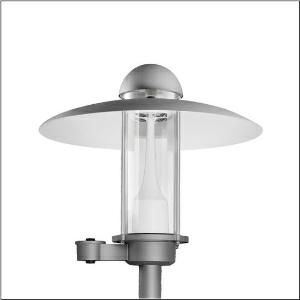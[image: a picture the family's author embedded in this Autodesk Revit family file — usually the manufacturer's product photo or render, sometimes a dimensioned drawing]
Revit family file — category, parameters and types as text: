
# Revit family: city-light_elegance___st1_2a_5xa5263er14h000032_c7d7
name_source: partatom
category: Lighting Fixtures
units: mm (PartAtom-declared; Revit-internal decimal feet)

## family parameters
Cut with Voids When Loaded = No
Host = Face
Light Source = No
Part Type = Normal
Room Calculation Point = No
Round Connector Dimension = Use Diameter
Shared = No

## types (1)
- --- (1 x LED, 1470 lm, 14.2 W, 3000K)
    Apparent Load = 14 VA
    CIE Flux Codes = 22 62 94 98 100
    Color Rendering = 80
    Color Temperature = 3000K
    Default Elevation = 1800 mm
    Description = City-Light Elegance, mast luminaire, Module 540 Plus, primary light control with 3 zone facetted reflector, of plastic, silver coated, highly specular, structured, primary optical cover: cover, of PMMA, transparent, light distribution: ST1.2a, light emission: direct distribution, primary light characteristic: asymmetric, installation type: post-top, LED, High Power LED, rated luminous flux: 1.470lm, luminous efficacy: 104lm/W, light colour: 830, colour temperature: 3000K, control gear: ECG Smart Interface, control: overheat protection, digital communication interface, time-dependent luminous flux control, flexible luminous flux parameterisation, presetting dimming logarithmic, with terminal, 6-pole, max. 2.5mm², mains connection: 230..240V, AC, 50/60Hz, start of lifetime: 14W, end of service life: 15W, reduction: 8W, luminaire housing, upper part, of aluminium, coated, Siteco® metallic grey (DB 702S), diameter: 750mm, height: 675mm, spigot size: d x l = 76 x 70mm (post-top) | with reducer (optional accessory) 60 x 70mm, post-top mast mounting element, of diecast aluminium, coated, Siteco® metallic grey (DB 702S), Module 540 Plus, traffic white (RAL 9016), Smart Interface below, protection rating (complete): IP65, insulation class (complete): insulation class II (safety insulation), certification: CE, ENEC, VDE, packaging unit: 1 piece

Light Distribution: ST1.2a
    Height = 675 mm
    Lamp = 1 x LED
    Lamp Light Flux = 1470 lm
    Lamp Power = 14.2 W
    Lamp count = 1
    Length = 750 mm
    Luminous efficacy = 104 lm/W
    Manufacturer = Siteco
    ModVariant = No
    Model = 5XA5263ER14H000032
    Number of Poles = 1
    OnlyDefault = Yes
    Power Factor = 1
    Product Name = City-Light Elegance | ST1.2a
    Product group = mast luminaire | pylon top
    ProductGroupID = 6100
    Protection Class = Protection class II
    Protection Degree = IP 65
    RLX_Detail_Level = 1
    RLX_Emergency_Light_Flux = 0 lm
    RLX_Emergency_Type = 0
    RLX_Emergency_Type_DB = No
    RlxData = <blob elided: 72729 chars, md5=fc4e0b91>
    Socket = socket
    Standby Power = 0 W
    System Light Flux = 1470 lm
    System Power = 14 W
    Type Comments = factory setting: luminous flux: 100 % | dim-lin: 254 | 516 mA
    Type Image = l_1005991.jpg
    URL = http://relux.com
    VarID = @adj_151447
    Voltage = 0 V
    Weight = 0.00 kg
    Width = 0 mm  [stored 0 ft]

note: [stored X ft] marks values corroborated as IEEE doubles in the binary element streams (Revit-internal decimal feet)

## geometry (parser evidence)
native form markers: Blend x4, Sweep x8
no freeform markers — native parametric forms only
